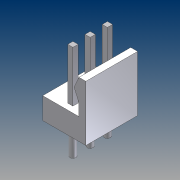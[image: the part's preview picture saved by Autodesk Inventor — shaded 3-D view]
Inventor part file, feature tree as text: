
AUTODESK INVENTOR PART (.ipt)
format: ipt  version: unknown  size: 203,776 bytes
history: native  units: mm (DEFAULTED — no unit token found)
features: extrude x3, plane x3, sketch x2, pattern_linear x1
ambient origin geometry x5: Origin, X Axis, Y Axis, Z Axis, Center Point
feature tree (9):
  extrude  "Extrusion1"  Depth=3.175mm
  sketch  "Sketch3"  dims[d2=8.1788mm d3=1.4478mm d4=1.016mm d5=2.54mm d6=0.0mm d7=0.762mm d8=3.556mm d9=0.0mm d10=10.668mm d11=0.0mm d12=30.0mm d14=2.54mm d15=0.889mm]
  extrude  "Extrusion2"  Depth=1.4478mm
  extrude  "Extrusion3"  Depth=1.016mm
  pattern_linear  "Rectangular Pattern1"  Spacing1=2.54mm  [1 undecoded]
  plane  "YZ Plane (RIGHT)"
  plane  "XZ Plane (TOP)"
  plane  "XY Plane (FRONT)"
  sketch  "Sketch2"  dims[d0=6.35mm d1=3.175mm]
note: 1 required parameter value undecoded (feature->parameter linkage not recoverable at this tier; creation-order binding heuristic only, values carry confidence <= 0.55)
